# Revit family: Valvula de Check
name_source: partatom
category: Pipe Accessories
units: mm (PartAtom-declared; Revit-internal decimal feet)

## family parameters
Always vertical = Yes
Cut with Voids When Loaded = No
Part Type = Breaks Into
Round Connector Dimension = Use Diameter
Shared = No
Work Plane-Based = No

## types (2) — shared parameters
Description = CHECK ANTIFRAUDE DZR PCP
Imagen = https://pcpplasticos.co
Manufacturer = PCP PLASTICOS
URL = https://pcpplasticos.co
zero-valued in all types: Default Elevation

## per-type parameters (varying)
| type | 1/2" | 3/4" | D | Model | SKU | d1 | d2 |
| Diametro 1/2" | Yes | No | 13 mm | 3380 | 3380 | 29 mm | 28 mm  [stored 0.0918635 ft] |
| Diametro 3/4" | No | Yes | 19 mm | 3381 | 3381 | 36 mm  [stored 0.11811 ft] | 35 mm |

note: [stored X ft] marks values corroborated as IEEE doubles in the binary element streams (Revit-internal decimal feet)

## geometry (parser evidence)
native form markers: Sweep x3
no freeform markers — native parametric forms only
